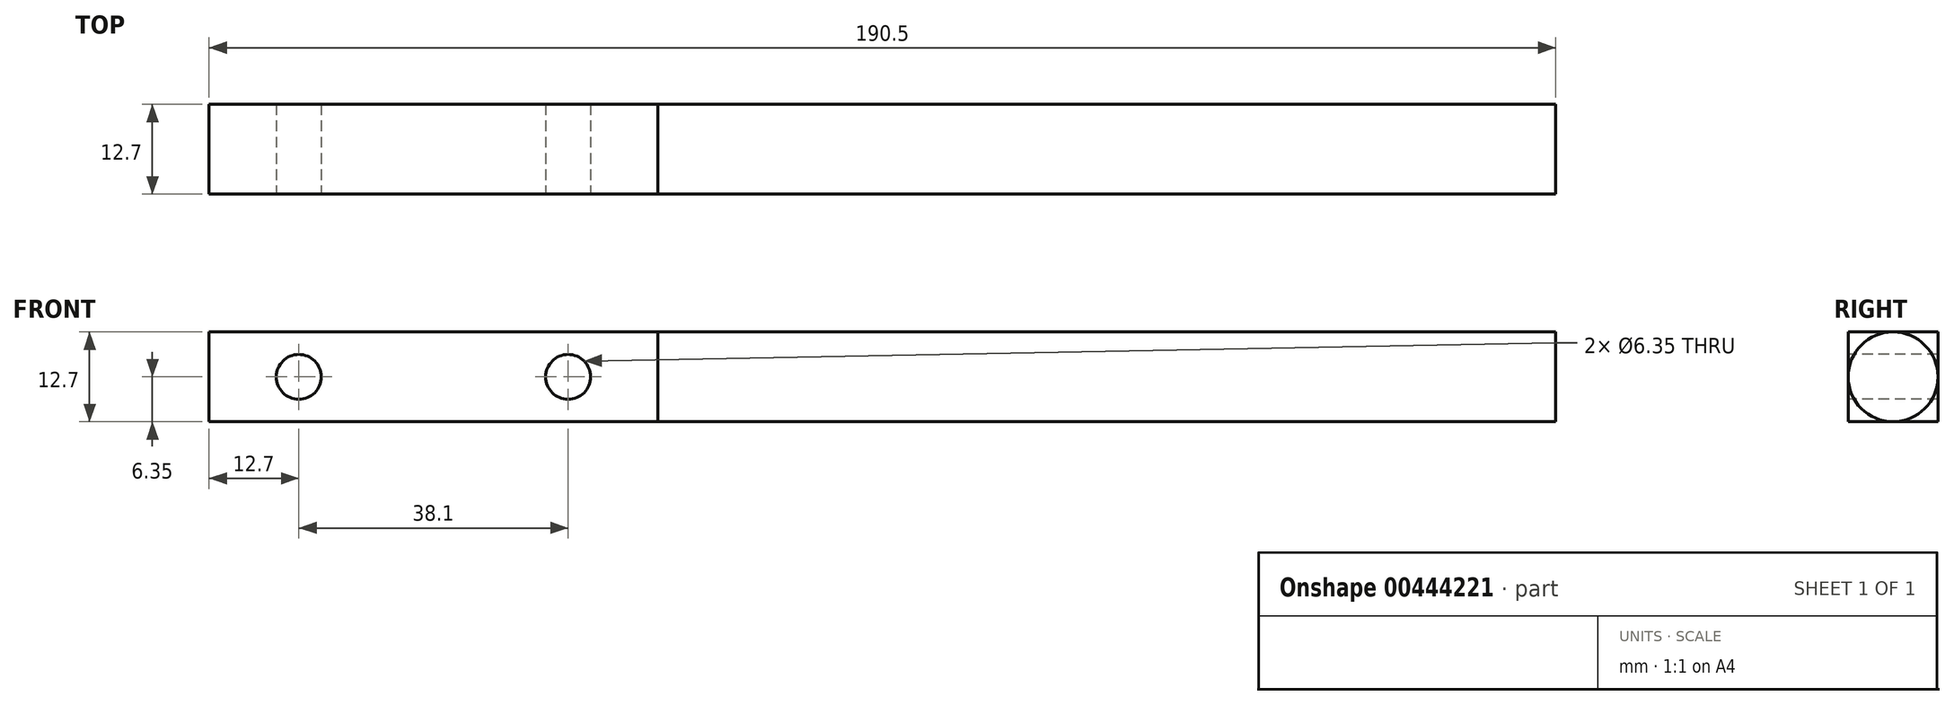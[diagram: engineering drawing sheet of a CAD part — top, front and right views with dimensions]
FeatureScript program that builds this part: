
annotation { "Feature Type Name" : "Feature", "Feature Type Description" : "" }
export const myFeature = defineFeature(function(context is Context, id is Id, definition is map)
    precondition{}
    {
        {
            var Q0;
            Q0=qCreatedBy(makeId("Right.planeOp"),FACE);
            var sketch = newSketch(context, id + "F0", { "sketchPlane" : qUnion([Q0])});
            skLineSegment(sketch, "E0.bottom", {"start": v(-6.35, 6.35) * mm, "end": v(6.35, 6.35) * mm});
            skLineSegment(sketch, "E0.top", {"start": v(-6.35, -6.35) * mm, "end": v(6.35, -6.35) * mm});
            skLineSegment(sketch, "E0.left", {"start": v(-6.35, 6.35) * mm, "end": v(-6.35, -6.35) * mm});
            skLineSegment(sketch, "E0.right", {"start": v(6.35, 6.35) * mm, "end": v(6.35, -6.35) * mm});
            skSolve(sketch);
        }
        {
            var Q0;
            Q0 = qSketchRegion(id + "F0", true);
            extrude(context, id + "F1", {"entities" : qUnion([Q0]), "depth" : 63.5 * mm});
        }
        {
            var Q0;
            Q0=makeQuery(id+"F1.opExtrude","CAP_FACE",FACE,{"disambiguationData":[OSD([sQuery(id+"F0.wireOp",EDGE,"E0.bottom"),sQuery(id+"F0.wireOp",EDGE,"E0.top"),sQuery(id+"F0.wireOp",EDGE,"E0.left"),sQuery(id+"F0.wireOp",EDGE,"E0.right")])],"isStart":false});
            var sketch = newSketch(context, id + "F2", { "sketchPlane" : qUnion([Q0])});
            skCircle(sketch, "E1", {"center": v(0, 0) * mm, "radius": 6.35 * mm});
            skSolve(sketch);
        }
        {
            var Q0;
            Q0 = qSketchRegion(id + "F2", true);
            extrude(context, id + "F3", {"entities" : qUnion([Q0]), "operationType" : NewBodyOperationType.ADD, "depth" : 127 * mm});
        }
        {
            var Q0;
            Q0=makeQuery(id+"F1.opExtrude","SWEPT_FACE",FACE,{"disambiguationData":[OSD([sQuery(id+"F0.wireOp",EDGE,"E0.left")])]});
            var sketch = newSketch(context, id + "F4", { "sketchPlane" : qUnion([Q0])});
            skLineSegment(sketch, "E2", {"start": v(12.7, 31.24) * mm, "end": v(12.7, -31.24) * mm});
            skLineSegment(sketch, "E3", {"start": v(50.8, 44.57) * mm, "end": v(50.8, -44.57) * mm});
            skCircle(sketch, "E4", {"center": v(12.7, 0) * mm, "radius": 3.18 * mm});
            skCircle(sketch, "E5", {"center": v(50.8, 0) * mm, "radius": 3.18 * mm});
            skSolve(sketch);
        }
        {
            var Q0;
            Q0 = qSketchRegion(id + "F4", true);
            extrude(context, id + "F5", {"entities" : qUnion([Q0]), "operationType" : NewBodyOperationType.REMOVE, "endBound" : BoundingType.THROUGH_ALL, "oppositeDirection" : true, "depth" : 25.4 * mm});
        }
    });
